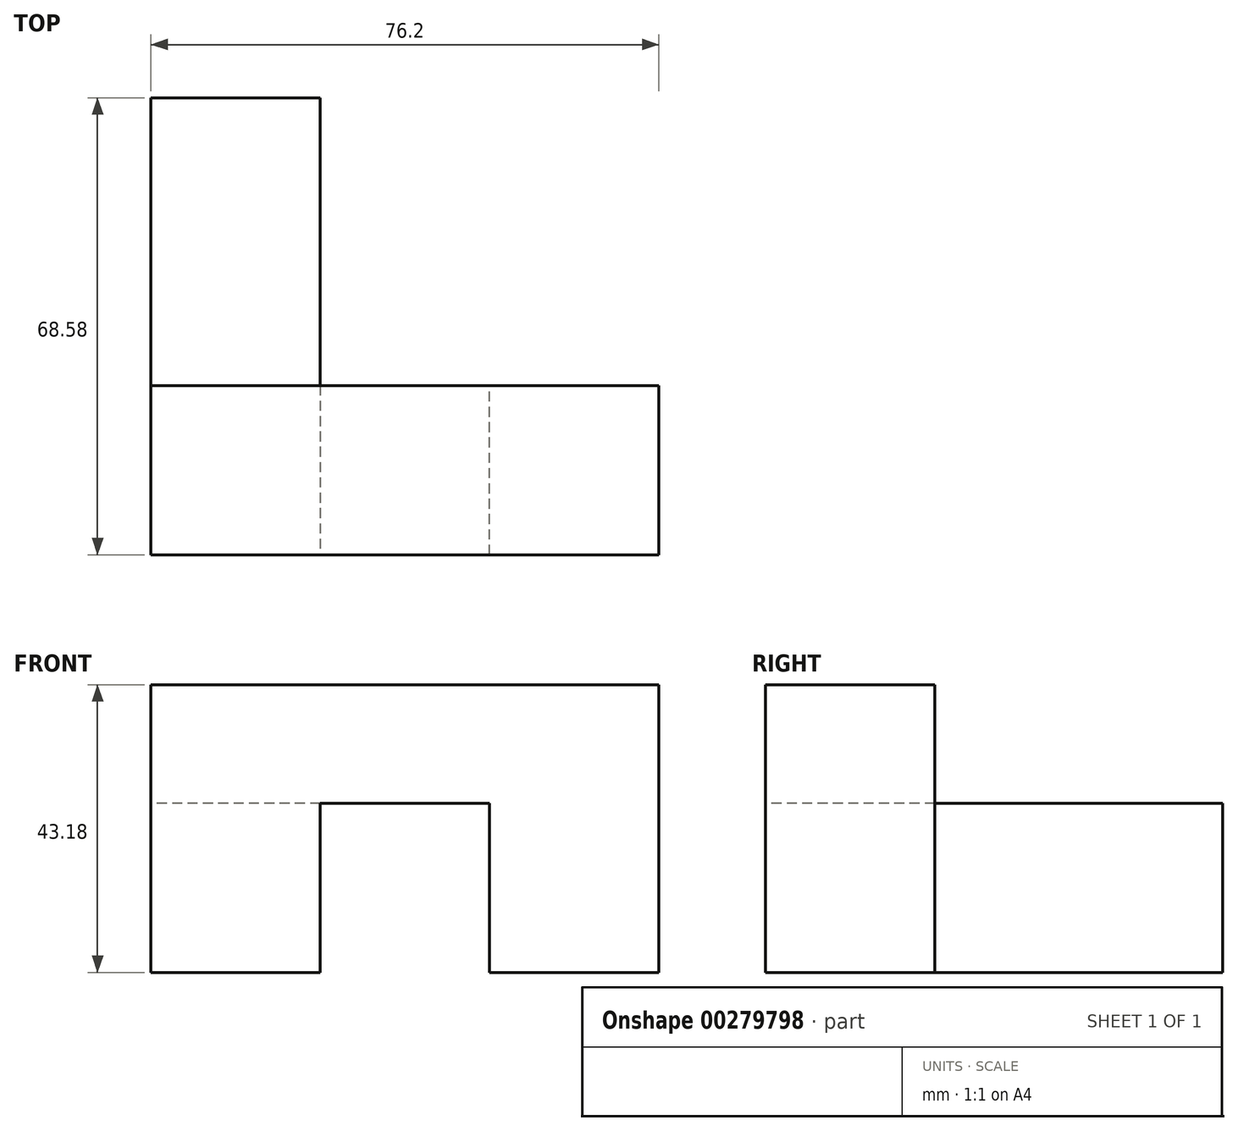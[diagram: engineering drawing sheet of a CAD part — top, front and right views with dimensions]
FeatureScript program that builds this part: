
annotation { "Feature Type Name" : "Feature", "Feature Type Description" : "" }
export const myFeature = defineFeature(function(context is Context, id is Id, definition is map)
    precondition{}
    {
        {
            var Q0;
            Q0=qCreatedBy(makeId("Right.planeOp"),FACE);
            var sketch = newSketch(context, id + "F0", { "sketchPlane" : qUnion([Q0])});
            skLineSegment(sketch, "E0.bottom", {"start": v(77.46, 31.62) * mm, "end": v(8.88, 31.62) * mm});
            skLineSegment(sketch, "E0.top", {"start": v(77.46, 6.22) * mm, "end": v(8.88, 6.22) * mm});
            skLineSegment(sketch, "E0.left", {"start": v(77.46, 31.62) * mm, "end": v(77.46, 6.22) * mm});
            skLineSegment(sketch, "E0.right", {"start": v(8.88, 31.62) * mm, "end": v(8.88, 6.22) * mm});
            skSolve(sketch);
        }
        {
            var Q0;
            Q0=makeQuery(id+"F0.imprint","IMPRINT",FACE,{"disambiguationData":[TD([[makeQuery(id+"F0.imprint","IMPRINT",EDGE,{"derivedFrom":sQuery(id+"F0.wireOp",EDGE,"E0.bottom")}),1.0]])]});
            extrude(context, id + "F1", {"entities" : qUnion([Q0]), "depth" : 25.4 * mm});
        }
        {
            var Q0;
            Q0=makeQuery(id+"F1.opExtrude","SWEPT_FACE",FACE,{"disambiguationData":[OSD([sQuery(id+"F0.wireOp",EDGE,"E0.bottom")])]});
            var sketch = newSketch(context, id + "F2", { "sketchPlane" : qUnion([Q0])});
            skLineSegment(sketch, "E1", {"start": v(25.4, 34.28) * mm, "end": v(0, 34.28) * mm});
            skSolve(sketch);
        }
        {
            var Q0;
            {var subQ0=sQuery(id+"F2.wireOp",EDGE,"E1");Q0=makeQuery(id+"F2.imprint","IMPRINT",FACE,{"disambiguationData":[TD([[makeQuery(id+"F2.imprint","IMPRINT",EDGE,{"derivedFrom":subQ0}),1.0]])]});}
            extrude(context, id + "F3", {"entities" : qUnion([Q0]), "operationType" : NewBodyOperationType.ADD, "depth" : 17.78 * mm});
        }
        {
            var Q0;
            {var subQ0=sQuery(id+"F0.wireOp",EDGE,"E0.bottom");var subQ1=makeQuery(id+"F1.opExtrude","CAP_EDGE",EDGE,{"disambiguationData":[OSD([subQ0])],"isStart":false});var subQ2=sQuery(id+"F0.wireOp",EDGE,"E0.right");Q0=makeQuery(id+"F3.boolean.opBoolean","MERGE",FACE,{"derivedFrom":[makeQuery(id+"F1.opExtrude","CAP_FACE",FACE,{"disambiguationData":[OSD([subQ0,sQuery(id+"F0.wireOp",EDGE,"E0.top"),sQuery(id+"F0.wireOp",EDGE,"E0.left"),subQ2])],"isStart":false}),makeQuery(id+"F3.opExtrude","SWEPT_FACE",FACE,{"disambiguationData":[OSD([subQ0]),TDD([makeQuery(id+"F2.imprint","IMPRINT",EDGE,{"disambiguationData":[TD([[makeQuery(id+"F2.imprint","INTERSECT",VERTEX,{"derivedFrom":[subQ1,sQuery(id+"F2.wireOp",EDGE,"E1")]}),-1.0]])],"derivedFrom":subQ1})])]})]});}
            var sketch = newSketch(context, id + "F4", { "sketchPlane" : qUnion([Q0])});
            skLineSegment(sketch, "E2", {"start": v(34.28, 31.62) * mm, "end": v(8.88, 31.62) * mm});
            skSolve(sketch);
        }
        {
            var Q0;
            {var subQ0=sQuery(id+"F4.wireOp",EDGE,"E2");Q0=makeQuery(id+"F4.imprint","IMPRINT",FACE,{"disambiguationData":[TD([[makeQuery(id+"F4.imprint","IMPRINT",EDGE,{"derivedFrom":subQ0}),-1.0]])]});}
            extrude(context, id + "F5", {"entities" : qUnion([Q0]), "operationType" : NewBodyOperationType.ADD, "depth" : 50.8 * mm});
        }
        {
            var Q0;
            Q0=makeQuery(id+"F5.opExtrude","SWEPT_FACE",FACE,{"disambiguationData":[OSD([sQuery(id+"F4.wireOp",EDGE,"E2")])]});
            var sketch = newSketch(context, id + "F6", { "sketchPlane" : qUnion([Q0])});
            skLineSegment(sketch, "E3", {"start": v(50.8, -8.88) * mm, "end": v(50.8, -34.28) * mm});
            skSolve(sketch);
        }
        {
            var Q0;
            {var subQ0=sQuery(id+"F6.wireOp",EDGE,"E3");Q0=makeQuery(id+"F6.imprint","IMPRINT",FACE,{"disambiguationData":[TD([[makeQuery(id+"F6.imprint","IMPRINT",EDGE,{"derivedFrom":subQ0}),1.0]])]});}
            extrude(context, id + "F7", {"entities" : qUnion([Q0]), "operationType" : NewBodyOperationType.ADD, "depth" : 25.4 * mm});
        }
    });
